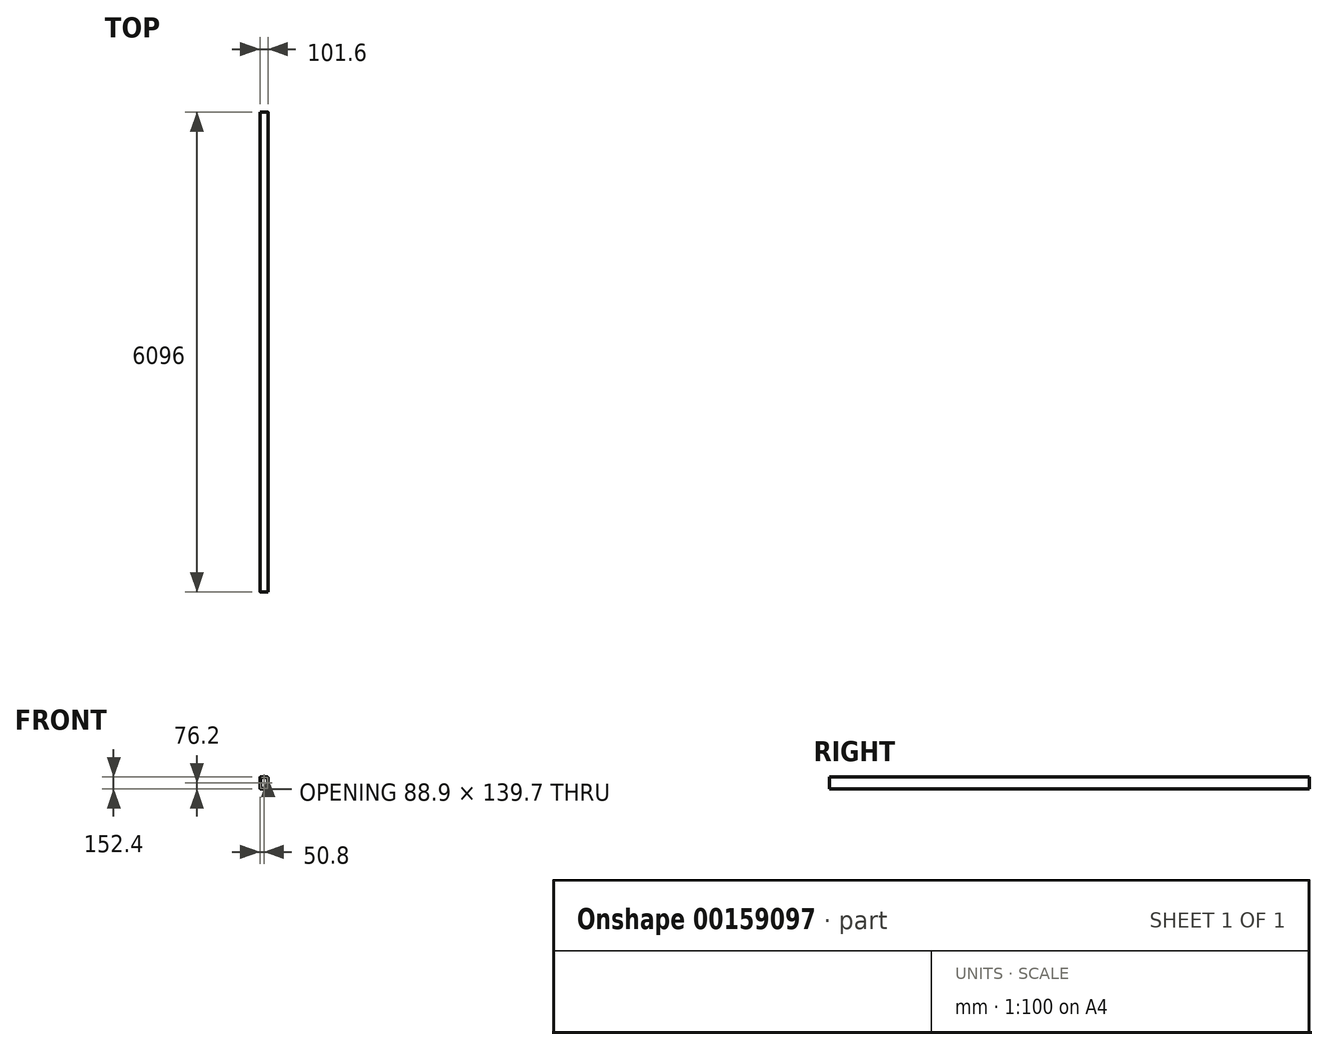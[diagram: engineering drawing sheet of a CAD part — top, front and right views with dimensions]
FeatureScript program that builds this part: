
annotation { "Feature Type Name" : "Feature", "Feature Type Description" : "" }
export const myFeature = defineFeature(function(context is Context, id is Id, definition is map)
    precondition{}
    {
        {
            var Q0;
            Q0=qCreatedBy(makeId("Front.planeOp"),FACE);
            var sketch = newSketch(context, id + "F0", { "sketchPlane" : qUnion([Q0])});
            skLineSegment(sketch, "E0.bottom", {"start": v(-42.86, 76.2) * mm, "end": v(42.86, 76.2) * mm});
            skLineSegment(sketch, "E0.top", {"start": v(-42.86, -76.2) * mm, "end": v(42.86, -76.2) * mm});
            skLineSegment(sketch, "E0.left", {"start": v(-50.8, 68.26) * mm, "end": v(-50.8, -68.26) * mm});
            skLineSegment(sketch, "E0.right", {"start": v(50.8, 68.26) * mm, "end": v(50.8, -68.26) * mm});
            skPoint(sketch, "E1.visualSharp", {"position": v(-50.8, 76.2) * mm});
            skArc(sketch, "E1.filletArc", {"start": v(-42.86, 76.2) * mm, "mid": v(-48.48, 73.88) * mm, "end": v(-50.8, 68.26) * mm});
            skPoint(sketch, "E2.visualSharp", {"position": v(-50.8, -76.2) * mm});
            skArc(sketch, "E2.filletArc", {"start": v(-50.8, -68.26) * mm, "mid": v(-48.48, -73.88) * mm, "end": v(-42.86, -76.2) * mm});
            skPoint(sketch, "E3.visualSharp", {"position": v(50.8, -76.2) * mm});
            skArc(sketch, "E3.filletArc", {"start": v(42.86, -76.2) * mm, "mid": v(48.48, -73.88) * mm, "end": v(50.8, -68.26) * mm});
            skPoint(sketch, "E4.visualSharp", {"position": v(50.8, 76.2) * mm});
            skArc(sketch, "E4.filletArc", {"start": v(50.8, 68.26) * mm, "mid": v(48.48, 73.88) * mm, "end": v(42.86, 76.2) * mm});
            skArc(sketch, "E5.0", {"start": v(-42.86, 69.85) * mm, "mid": v(-43.99, 69.39) * mm, "end": v(-44.45, 68.26) * mm});
            skLineSegment(sketch, "E5.1", {"start": v(-42.86, 69.85) * mm, "end": v(42.86, 69.85) * mm});
            skLineSegment(sketch, "E5.2", {"start": v(-44.45, 68.26) * mm, "end": v(-44.45, -68.26) * mm});
            skArc(sketch, "E5.3", {"start": v(44.45, 68.26) * mm, "mid": v(43.99, 69.39) * mm, "end": v(42.86, 69.85) * mm});
            skArc(sketch, "E5.4", {"start": v(-44.45, -68.26) * mm, "mid": v(-43.99, -69.39) * mm, "end": v(-42.86, -69.85) * mm});
            skLineSegment(sketch, "E5.5", {"start": v(-42.86, -69.85) * mm, "end": v(42.86, -69.85) * mm});
            skArc(sketch, "E5.6", {"start": v(42.86, -69.85) * mm, "mid": v(43.99, -69.39) * mm, "end": v(44.45, -68.26) * mm});
            skLineSegment(sketch, "E5.7", {"start": v(44.45, 68.26) * mm, "end": v(44.45, -68.26) * mm});
            skSolve(sketch);
        }
        {
            var Q0;
            Q0=makeQuery(id+"F0.imprint","IMPRINT",FACE,{"disambiguationData":[TD([[makeQuery(id+"F0.imprint","IMPRINT",EDGE,{"derivedFrom":sQuery(id+"F0.wireOp",EDGE,"E0.bottom")}),-1.0]])]});
            extrude(context, id + "F1", {"entities" : qUnion([Q0]), "endBound" : BoundingType.SYMMETRIC, "depth" : 6096 * mm});
        }
    });
